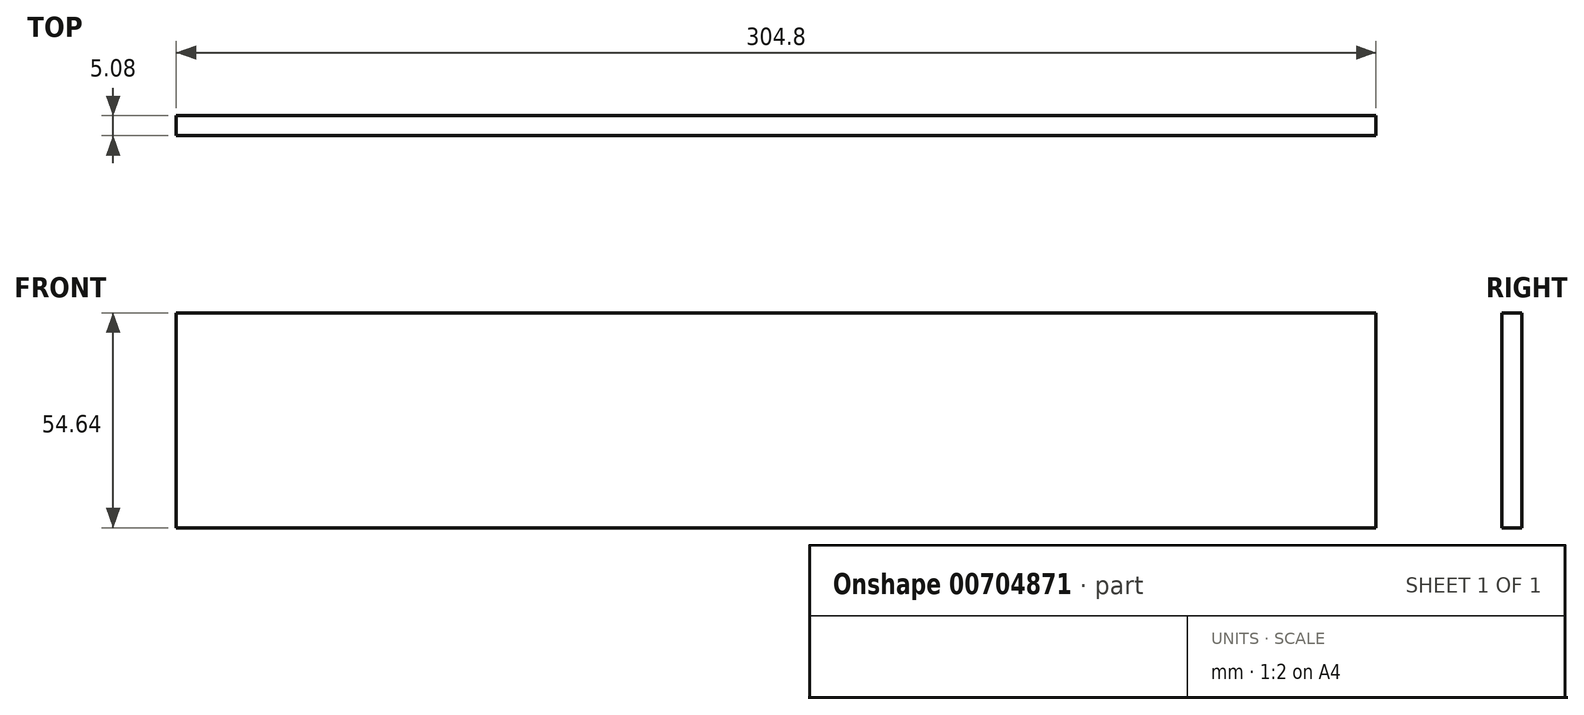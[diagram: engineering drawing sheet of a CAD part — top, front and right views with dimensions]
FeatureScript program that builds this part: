
annotation { "Feature Type Name" : "Feature", "Feature Type Description" : "" }
export const myFeature = defineFeature(function(context is Context, id is Id, definition is map)
    precondition{}
    {
        {
            var Q0;
            Q0=qCreatedBy(makeId("Front.planeOp"),FACE);
            var sketch = newSketch(context, id + "F0", { "sketchPlane" : qUnion([Q0])});
            skLineSegment(sketch, "E0.bottom", {"start": v(-82.72, 38.2) * mm, "end": v(222.08, 38.2) * mm});
            skLineSegment(sketch, "E0.top", {"start": v(-82.72, -16.43) * mm, "end": v(222.08, -16.43) * mm});
            skLineSegment(sketch, "E0.left", {"start": v(-82.72, 38.2) * mm, "end": v(-82.72, -16.43) * mm});
            skLineSegment(sketch, "E0.right", {"start": v(222.08, 38.2) * mm, "end": v(222.08, -16.43) * mm});
            skSolve(sketch);
        }
        {
            var Q0;
            Q0=makeQuery(id+"F0.imprint","IMPRINT",FACE,{"disambiguationData":[TD([[makeQuery(id+"F0.imprint","IMPRINT",EDGE,{"derivedFrom":sQuery(id+"F0.wireOp",EDGE,"E0.bottom")}),-1.0]])]});
            extrude(context, id + "F1", {"entities" : qUnion([Q0]), "depth" : 5.08 * mm, "offsetDistance" : 25.4 * mm});
        }
    });
